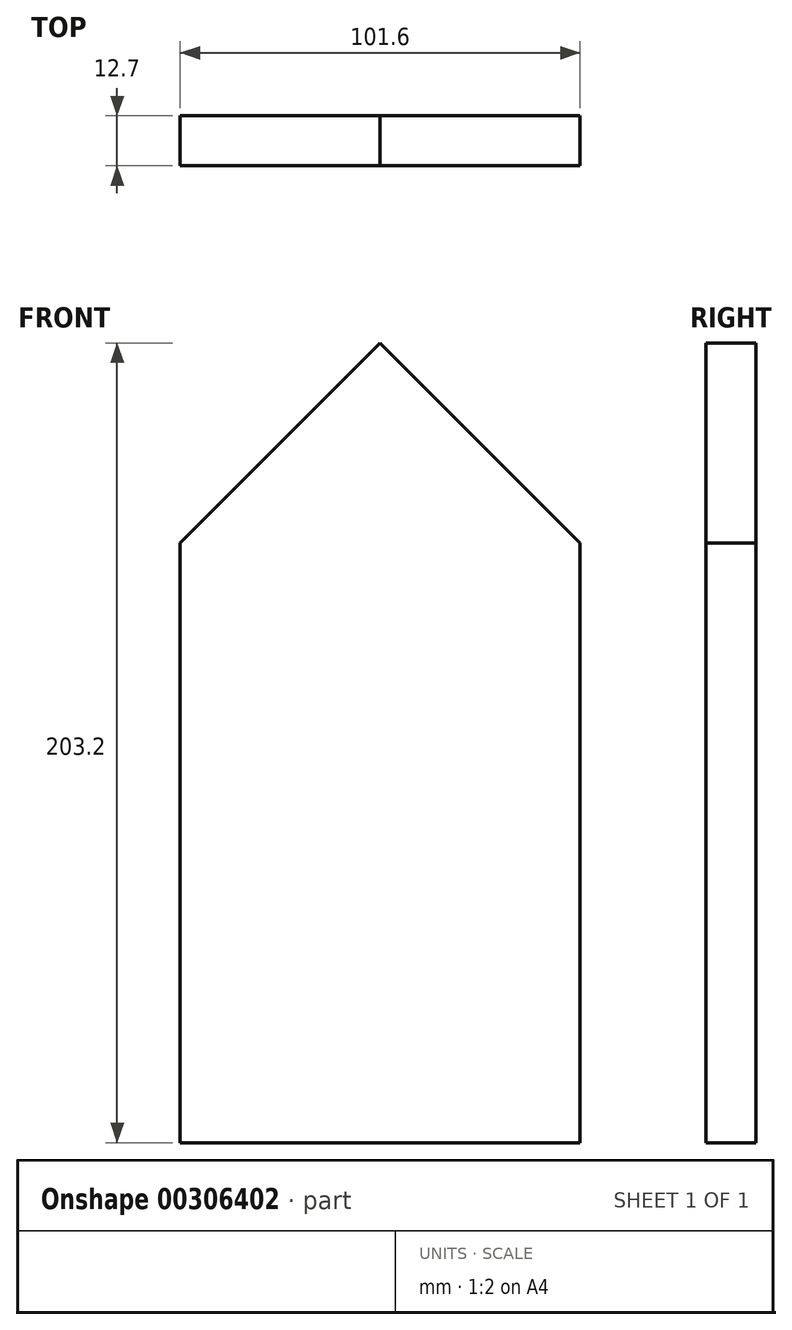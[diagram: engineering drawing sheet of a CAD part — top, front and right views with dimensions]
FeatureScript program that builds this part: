
annotation { "Feature Type Name" : "Feature", "Feature Type Description" : "" }
export const myFeature = defineFeature(function(context is Context, id is Id, definition is map)
    precondition{}
    {
        {
            var Q0;
            Q0=qCreatedBy(makeId("Front.planeOp"),FACE);
            var sketch = newSketch(context, id + "F0", { "sketchPlane" : qUnion([Q0])});
            skLineSegment(sketch, "E0.bottom", {"start": v(-50.8, -101.6) * mm, "end": v(50.8, -101.6) * mm});
            skLineSegment(sketch, "E0.top", {"start": v(-50.8, 101.6) * mm, "end": v(50.8, 101.6) * mm});
            skLineSegment(sketch, "E0.left", {"start": v(-50.8, -101.6) * mm, "end": v(-50.8, 101.6) * mm});
            skLineSegment(sketch, "E0.right", {"start": v(50.8, -101.6) * mm, "end": v(50.8, 101.6) * mm});
            skPoint(sketch, "E0.middle", {"position": v(0, 0) * mm});
            skLineSegment(sketch, "E1", {"start": v(50.8, 50.8) * mm, "end": v(0, 101.6) * mm});
            skLineSegment(sketch, "E2", {"start": v(0, 101.6) * mm, "end": v(-50.8, 50.8) * mm});
            skSolve(sketch);
        }
        {
            var Q0;
            {var subQ2=sQuery(id+"F0.wireOp",EDGE,"E0.bottom");Q0=makeQuery(id+"F0.imprint","IMPRINT",FACE,{"disambiguationData":[TD([[makeQuery(id+"F0.imprint","IMPRINT",EDGE,{"derivedFrom":subQ2}),1.0]])]});}
            extrude(context, id + "F1", {"entities" : qUnion([Q0]), "depth" : 12.7 * mm});
        }
    });
